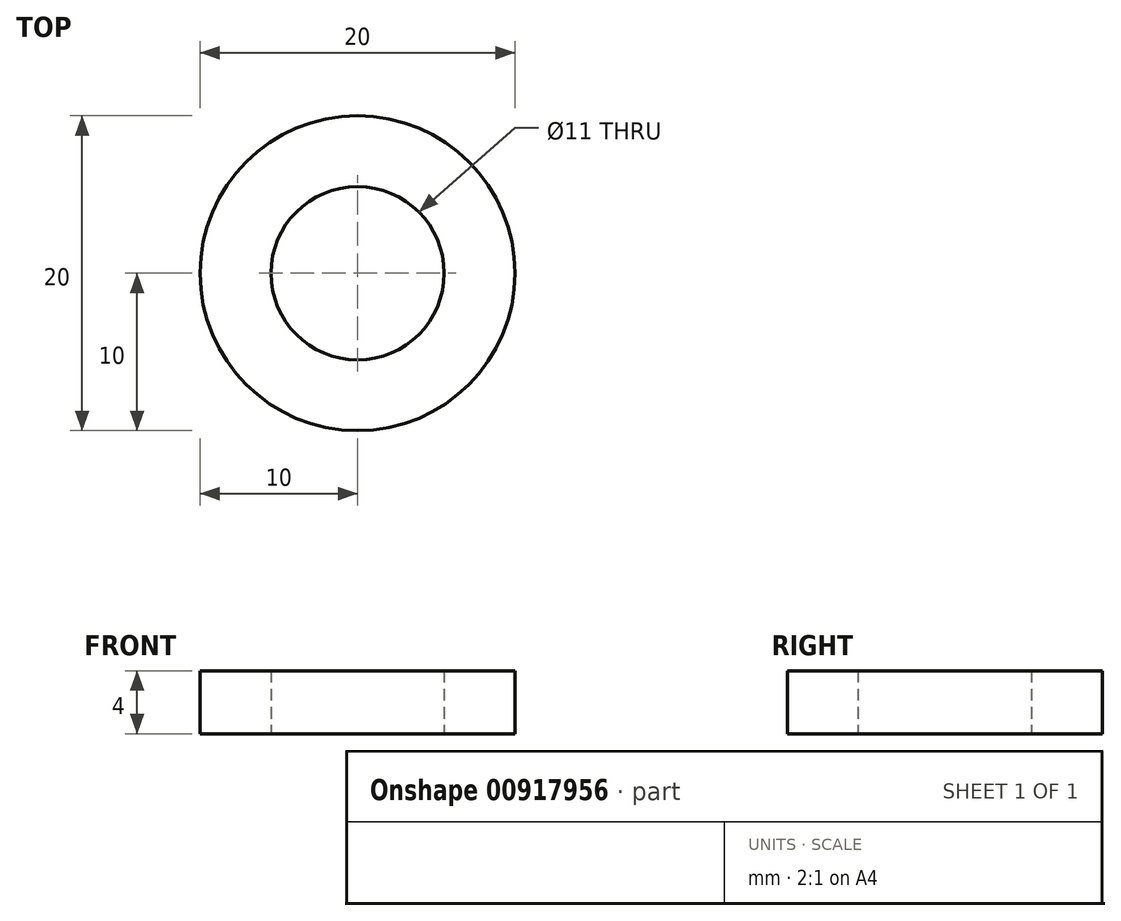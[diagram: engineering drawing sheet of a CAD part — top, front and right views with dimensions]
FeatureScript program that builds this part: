
annotation { "Feature Type Name" : "Feature", "Feature Type Description" : "" }
export const myFeature = defineFeature(function(context is Context, id is Id, definition is map)
    precondition{}
    {
        {
            var Q0;
            Q0=qCreatedBy(makeId("Top.planeOp"),FACE);
            var sketch = newSketch(context, id + "F0", { "sketchPlane" : qUnion([Q0])});
            skCircle(sketch, "E0", {"center": v(0, 0) * mm, "radius": 10 * mm});
            skSolve(sketch);
        }
        {
            var Q0;
            Q0=qCreatedBy(makeId("Top.planeOp"),FACE);
            var sketch = newSketch(context, id + "F1", { "sketchPlane" : qUnion([Q0])});
            skCircle(sketch, "E1", {"center": v(0, 0) * mm, "radius": 7.5 * mm});
            skSolve(sketch);
        }
        {
            var Q0;
            Q0=makeQuery(id+"F0.imprint","IMPRINT",FACE,{"disambiguationData":[TD([[makeQuery(id+"F0.imprint","IMPRINT",EDGE,{"derivedFrom":sQuery(id+"F0.wireOp",EDGE,"E0")}),1.0]])]});
            extrude(context, id + "F2", {"entities" : qUnion([Q0]), "depth" : 4 * mm, "offsetDistance" : 25.4 * mm});
        }
        {
            var Q0;
            Q0=sQuery(id+"F1.wireOp",VERTEX,"E1.center");
            var Q1;
            Q1=makeQuery(id+"F2.opExtrude","SWEPT_BODY",BODY,{"disambiguationData":[OSD([sQuery(id+"F0.wireOp",EDGE,"E0")])]});
            hole(context, id + "F3", {"style" : HoleStyle.SIMPLE, "endStyle" : HoleEndStyle.THROUGH, "oppositeDirection" : true, "holeDiameter" : 11 * mm, "majorDiameter" : 6.35 * mm, "isTappedThrough" : true, "tappedDepth" : 12.7 * mm, "tapClearance" : 3, "locations" : qUnion([Q0]), "scope" : qUnion([Q1])});
        }
    });
